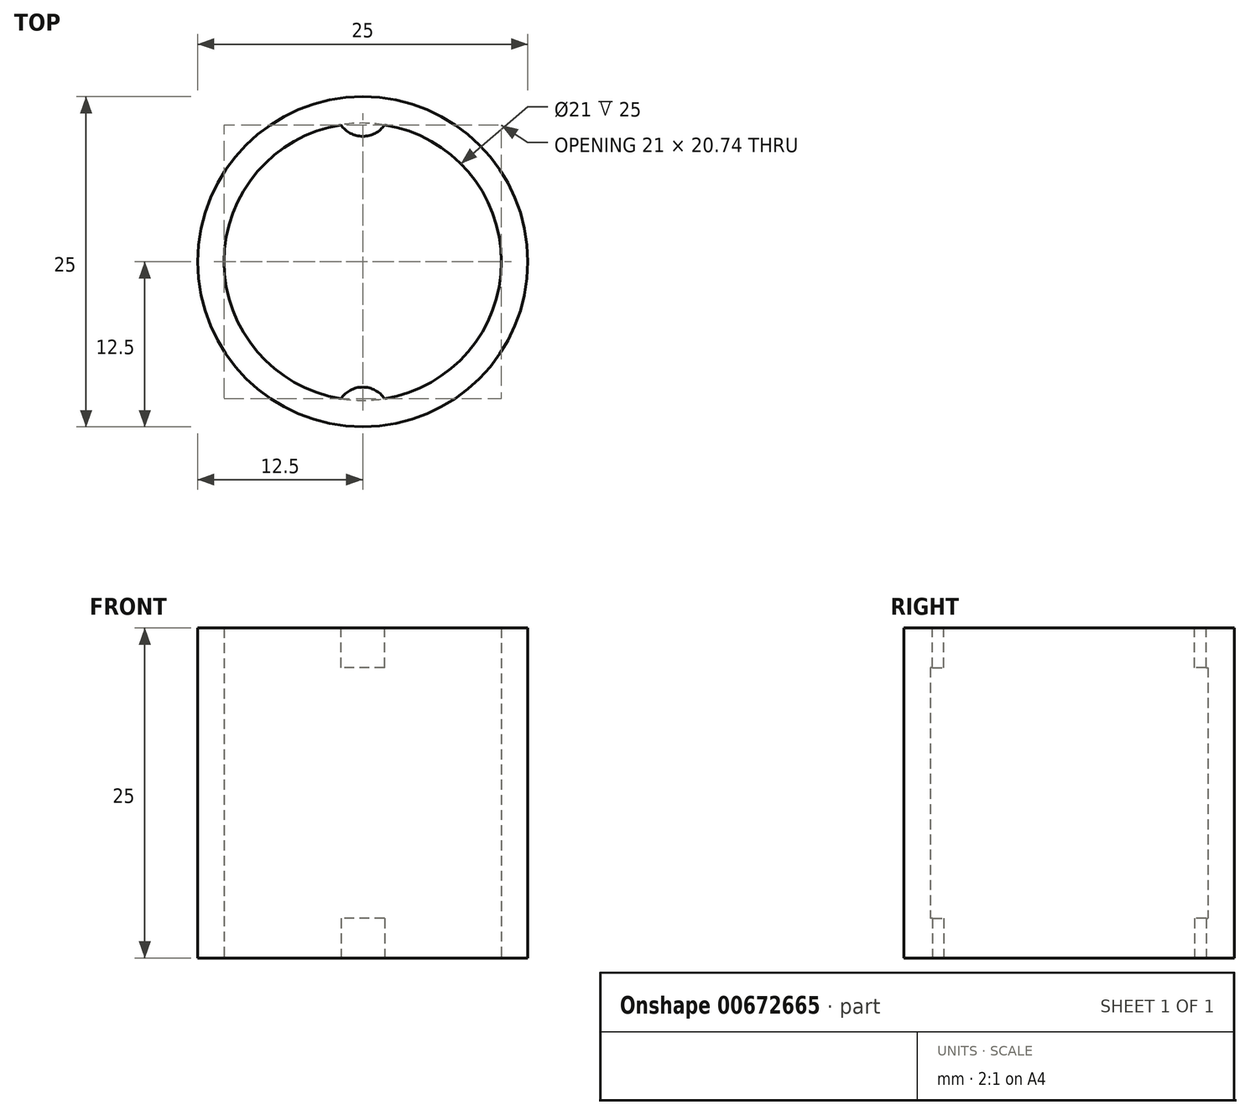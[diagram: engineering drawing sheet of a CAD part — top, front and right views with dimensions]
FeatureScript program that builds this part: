
annotation { "Feature Type Name" : "Feature", "Feature Type Description" : "" }
export const myFeature = defineFeature(function(context is Context, id is Id, definition is map)
    precondition{}
    {
        {
            var Q0;
            Q0=qCreatedBy(makeId("Top.planeOp"),FACE);
            var sketch = newSketch(context, id + "F0", { "sketchPlane" : qUnion([Q0])});
            skCircle(sketch, "E0", {"center": v(0, 0) * mm, "radius": 10.5 * mm});
            skCircle(sketch, "E1", {"center": v(0, 0) * mm, "radius": 12.5 * mm});
            skSolve(sketch);
        }
        {
            var Q0;
            Q0 = qSketchRegion(id + "F0", true);
            extrude(context, id + "F1", {"entities" : qUnion([Q0]), "depth" : 25 * mm, "offsetDistance" : 25 * mm});
        }
        {
            var Q0;
            Q0=makeQuery(id+"F1.opExtrude","CAP_FACE",FACE,{"disambiguationData":[OSD([sQuery(id+"F0.wireOp",EDGE,"E0"),sQuery(id+"F0.wireOp",EDGE,"E1")])],"isStart":true});
            var sketch = newSketch(context, id + "F2", { "sketchPlane" : qUnion([Q0])});
            skLineSegment(sketch, "E2", {"start": v(0, 10.5) * mm, "end": v(0, 12.5) * mm, "construction": true});
            skArc(sketch, "E3", {"start": v(-1.8, 12.37) * mm, "mid": v(0, 9.5) * mm, "end": v(1.8, 12.37) * mm});
            skArc(sketch, "E4", {"start": v(1.8, 12.37) * mm, "mid": v(0, 12.5) * mm, "end": v(-1.8, 12.37) * mm});
            skArc(sketch, "E5.MirrorCS", {"start": v(-1.8, -12.37) * mm, "mid": v(0, -9.5) * mm, "end": v(1.8, -12.37) * mm});
            skArc(sketch, "E6.MirrorCS", {"start": v(1.8, -12.37) * mm, "mid": v(0, -12.5) * mm, "end": v(-1.8, -12.37) * mm});
            skSolve(sketch);
        }
        {
            var Q0;
            Q0 = qSketchRegion(id + "F2", true);
            extrude(context, id + "F3", {"entities" : qUnion([Q0]), "operationType" : NewBodyOperationType.ADD, "oppositeDirection" : true, "depth" : 3 * mm, "offsetDistance" : 25 * mm});
        }
        {
            var Q0;
            Q0=makeQuery(id+"F1.opExtrude","CAP_FACE",FACE,{"disambiguationData":[OSD([sQuery(id+"F0.wireOp",EDGE,"E0"),sQuery(id+"F0.wireOp",EDGE,"E1")])],"isStart":false});
            var sketch = newSketch(context, id + "F4", { "sketchPlane" : qUnion([Q0])});
            skLineSegment(sketch, "E7", {"start": v(0, 10.5) * mm, "end": v(0, 12.5) * mm, "construction": true});
            skArc(sketch, "E8", {"start": v(-1.8, 12.37) * mm, "mid": v(0, 9.5) * mm, "end": v(1.8, 12.37) * mm});
            skArc(sketch, "E9", {"start": v(1.8, 12.37) * mm, "mid": v(0, 12.5) * mm, "end": v(-1.8, 12.37) * mm});
            skArc(sketch, "E10.MirrorCS", {"start": v(-1.8, -12.37) * mm, "mid": v(0, -9.5) * mm, "end": v(1.8, -12.37) * mm});
            skArc(sketch, "E11.MirrorCS", {"start": v(1.8, -12.37) * mm, "mid": v(0, -12.5) * mm, "end": v(-1.8, -12.37) * mm});
            skSolve(sketch);
        }
        {
            var Q0;
            Q0 = qSketchRegion(id + "F4", true);
            extrude(context, id + "F5", {"entities" : qUnion([Q0]), "operationType" : NewBodyOperationType.ADD, "oppositeDirection" : true, "depth" : 3 * mm, "offsetDistance" : 25 * mm});
        }
    });
